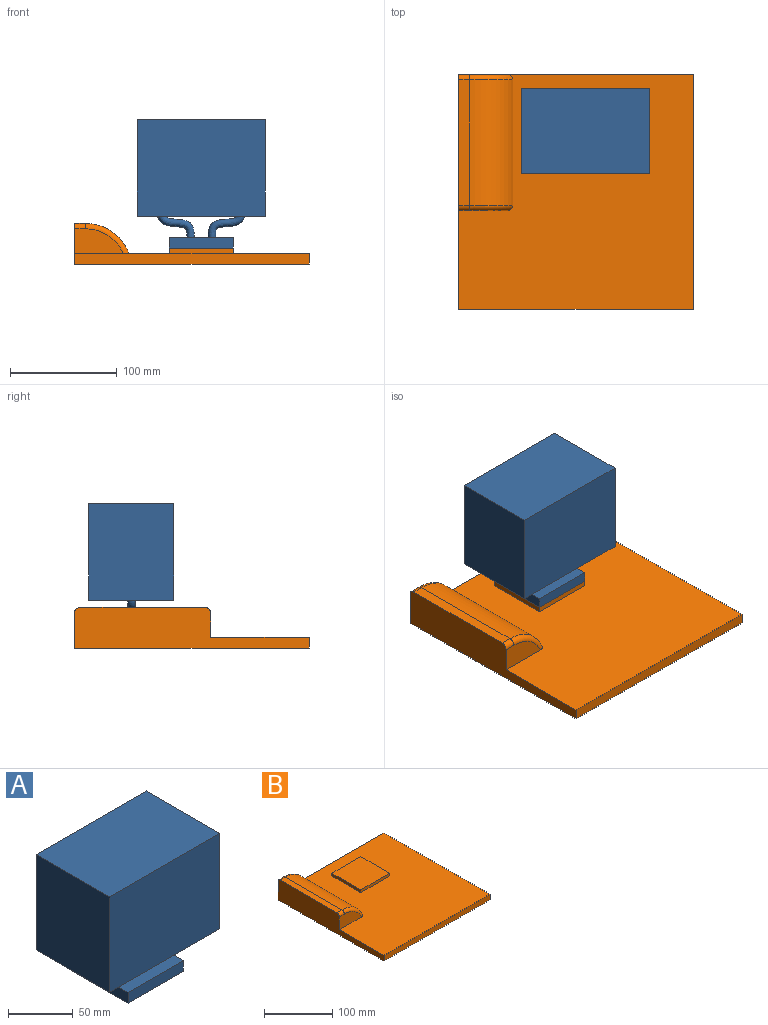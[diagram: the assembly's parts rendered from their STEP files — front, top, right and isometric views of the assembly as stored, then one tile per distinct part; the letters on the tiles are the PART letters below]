
ASSEMBLY  parts=2 mates=1
PART A: 18 faces, bbox 121.3x81.3x121.7 mm
  f0: bspline ~35.03x24.84mm, area 862.6mm2, adj f2,f14
  f1: bspline ~35.03x24.84mm, area 862.6mm2, adj f2,f14
  f2: plane 60.98x60.98mm, normal (0,0,1), area 3523.1mm2, adj f0,f1,f4,f5,f6,f7
  f3: plane 61.26x61.26mm, normal (0,0,-1), area 3561.9mm2, adj f4,f5,f6,f7,f8,f9,f10,f11
  f4: plane 60x10mm, normal (0,1,0), area 600mm2, adj f2,f3,f5,f7
  f5: plane 60x10mm, normal (-1,0,0), area 600mm2, adj f2,f3,f4,f6
  f6: plane 60x10mm, normal (0,-1,0), area 600mm2, adj f2,f3,f5,f7
  f7: plane 60x10mm, normal (1,0,0), area 600mm2, adj f2,f3,f4,f6
  f8: bspline ~7x3.42mm, area 0mm2, adj f3,f9
  f9: plane 7.98x4.41mm, normal (-0.14,0,-0.99), area 19mm2, adj f3,f8
  f10: bspline ~7x3.42mm, area 0mm2, adj f3,f11
  f11: plane 7.98x4.41mm, normal (0.14,0,-0.99), area 19mm2, adj f3,f10
  f12: plane 120x80mm, normal (0,0,1), area 9600mm2, adj f13,f15,f16,f17
  f13: plane 90x80mm, normal (-1,0,0), area 7200mm2, adj f12,f14,f16,f17
  f14: plane 120x80mm, normal (0,0,-1), area 9518.6mm2, adj f0,f1,f13,f15,f16,f17
  f15: plane 90x80mm, normal (1,0,0), area 7200mm2, adj f12,f14,f16,f17
  f16: plane 120x90mm, normal (0,-1,0), area 10800mm2, adj f12,f13,f14,f15
  f17: plane 120x90mm, normal (0,1,0), area 10800mm2, adj f12,f13,f14,f15
PART B: 18 faces, bbox 220x220x41.6 mm
  f0: plane 220x220mm, normal (0,0,1), area 38337.3mm2, adj f1,f2,f3,f4,f6,f8,f9,f11
  f1: plane 220x33mm, normal (0,1,0), area 3018.5mm2, adj f0,f2,f4,f5,f11,f12
  f2: plane 220x38mm, normal (-1,0,0), area 5755.7mm2, adj f0,f1,f3,f5,f6,f7,f10,f12
  f3: plane 220x10mm, normal (0,-1,0), area 2200mm2, adj f0,f2,f4,f5
  f4: plane 220x10mm, normal (1,0,0), area 2200mm2, adj f0,f1,f3,f5
  f5: plane 220x220mm, normal (0,0,-1), area 48400mm2, adj f1,f2,f3,f4
  f6: plane 45.43x23mm, normal (0,-1,0), area 818.5mm2, adj f0,f2,f9,f10
  f7: plane 117.37x10.22mm, normal (0,0,1), area 1199mm2, adj f2,f8,f10,f12
  f8: cylinder r=43.46mm len=117.37mm, axis (0,-1,0), area 6157.2mm2, adj f0,f7,f9,f11
  f9: torus R=38.46mm, axis (0,1,0), area 389.3mm2, adj f0,f6,f8,f10
  f10: cylinder r=5mm len=10.22mm, axis (-1,0,0), area 80.2mm2, adj f2,f6,f7,f9
  f11: torus R=38.46mm, axis (0,1,0), area 389.3mm2, adj f0,f1,f8,f12
  f12: cylinder r=5mm len=10.22mm, axis (1,0,0), area 80.2mm2, adj f1,f2,f7,f11
  f13: plane 60x5mm, normal (0,1,0), area 300mm2, adj f0,f14,f16,f17
  f14: plane 60x5mm, normal (-1,0,0), area 300mm2, adj f0,f13,f15,f17
  f15: plane 60x5mm, normal (0,-1,0), area 300mm2, adj f0,f14,f16,f17
  f16: plane 60x5mm, normal (1,0,0), area 300mm2, adj f0,f13,f15,f17
  f17: plane 60x60mm, normal (0,0,1), area 3600mm2, adj f13,f14,f15,f16
PLACE A t=(16.19,75.2,-53.79)mm
PLACE B t=(-72.43,98.32,-68.79)mm
MATE fastened A.f3 <-> B.f17  axis (0,0,-1) through (46.19,45.2,-53.79)mm
